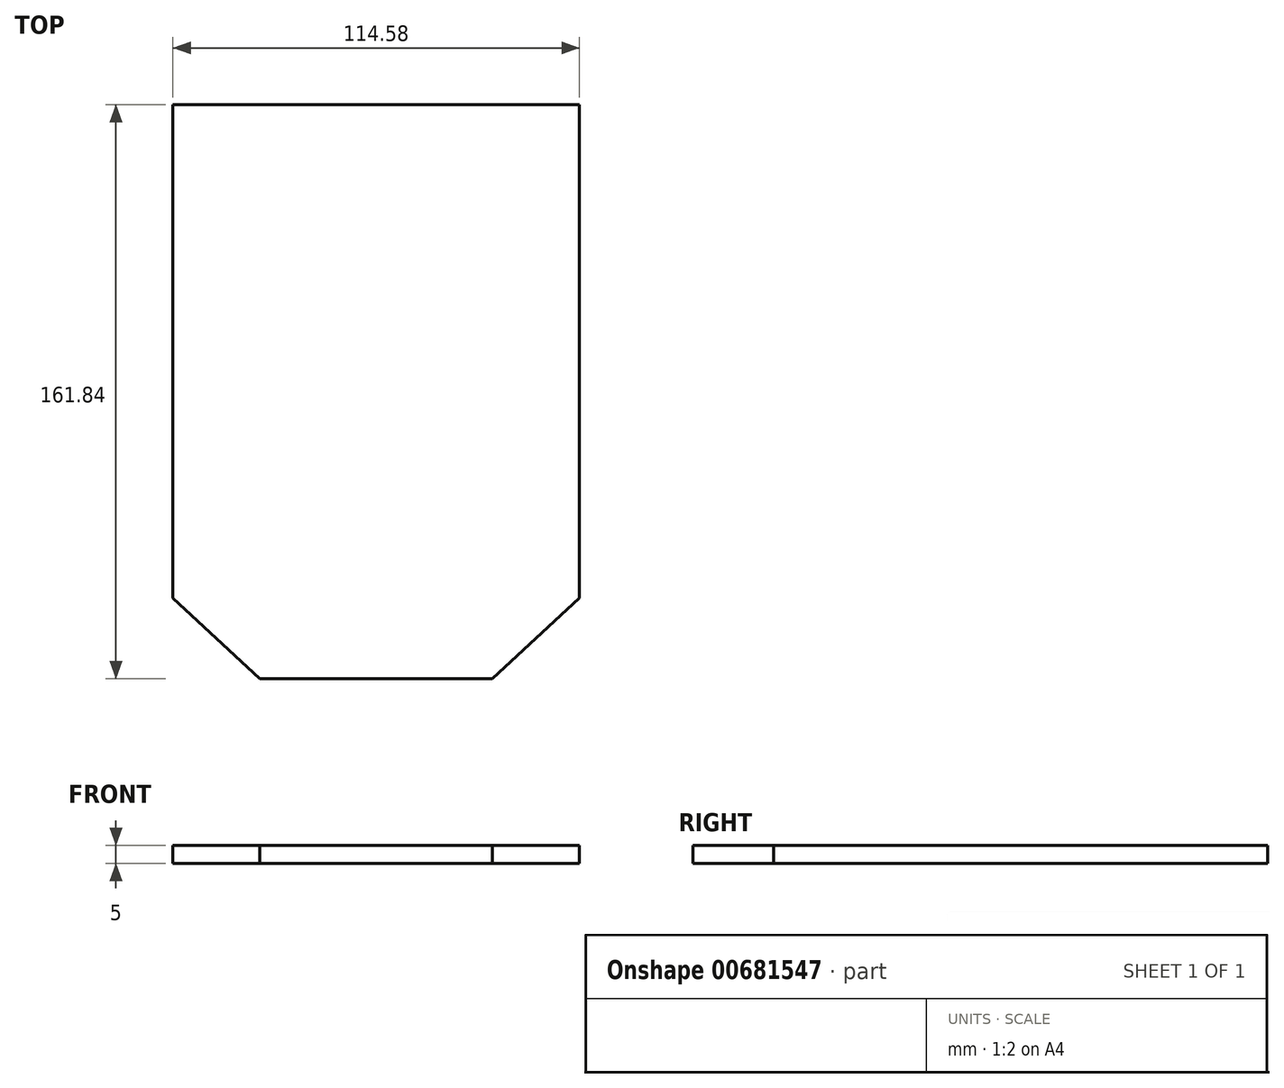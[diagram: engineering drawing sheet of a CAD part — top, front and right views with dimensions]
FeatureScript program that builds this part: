
annotation { "Feature Type Name" : "Feature", "Feature Type Description" : "" }
export const myFeature = defineFeature(function(context is Context, id is Id, definition is map)
    precondition{}
    {
        {
            var Q0;
            Q0=qCreatedBy(makeId("Top.planeOp"),FACE);
            var sketch = newSketch(context, id + "F0", { "sketchPlane" : qUnion([Q0])});
            skLineSegment(sketch, "E0", {"start": v(75.57, 76.01) * mm, "end": v(75.57, 87.16) * mm});
            skLineSegment(sketch, "E1", {"start": v(75.57, 87.16) * mm, "end": v(-39, 87.16) * mm});
            skLineSegment(sketch, "E2", {"start": v(-39, 87.16) * mm, "end": v(-39, -51.94) * mm});
            skLineSegment(sketch, "E3", {"start": v(-14.49, -74.68) * mm, "end": v(51.05, -74.68) * mm});
            skLineSegment(sketch, "E4", {"start": v(75.57, -51.94) * mm, "end": v(75.57, 76.01) * mm});
            skLineSegment(sketch, "E5", {"start": v(51.05, -74.68) * mm, "end": v(-14.49, -74.68) * mm});
            skLineSegment(sketch, "E6", {"start": v(-39, -51.94) * mm, "end": v(-14.49, -74.68) * mm});
            skLineSegment(sketch, "E7", {"start": v(75.57, -51.94) * mm, "end": v(51.05, -74.68) * mm});
            skPoint(sketch, "E8.start.orphan", {"position": v(-68.88, -74.68) * mm});
            skPoint(sketch, "E9.start.orphan", {"position": v(-14.49, -86.27) * mm});
            skPoint(sketch, "E10.orphan", {"position": v(-39, -74.68) * mm});
            skPoint(sketch, "E11.end.orphan", {"position": v(75.57, -86.27) * mm});
            skPoint(sketch, "E12.orphan", {"position": v(75.57, -74.68) * mm});
            skPoint(sketch, "E13.end.orphan", {"position": v(109, -51.94) * mm});
            skPoint(sketch, "E13.start.orphan", {"position": v(109, -74.68) * mm});
            skSolve(sketch);
        }
        {
            var Q0;
            Q0 = qSketchRegion(id + "F0", true);
            extrude(context, id + "F1", {"entities" : qUnion([Q0]), "depth" : 5 * mm, "offsetDistance" : 25 * mm});
        }
    });
